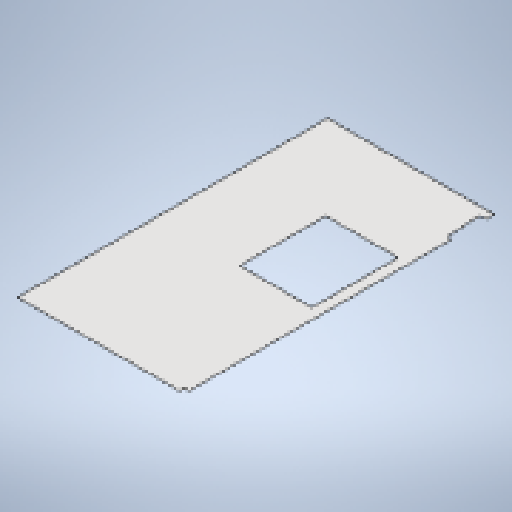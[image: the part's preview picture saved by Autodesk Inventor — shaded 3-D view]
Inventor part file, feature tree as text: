
AUTODESK INVENTOR PART (.ipt)
format: ipt  version: 2025.1 (Build 291241020, 241B)  size: 218,624 bytes
history: native  units: mm
features: other x2, sheet_metal_op x1, chamfer x1, sketch x1
ambient origin geometry x8: Origin, YZ Plane, XZ Plane, XY Plane, X Axis, Y Axis, Z Axis, Center Point
bodies: Body1 (feature_tree)
feature tree (5):
  sheet_metal_op  "Face3"
  chamfer  "Corner Round1"
  sketch  "Sketch1"  dims[d61=500.0mm d154=1385.0mm d155=2575.0mm d156=2.0mm d157=40.0mm d158=15.0mm d159=290.0mm d161=40.0mm d162=2220.0mm d163=10.0mm d164=150.0mm d165=5.0mm d166=590.0mm d167=590.0mm d168=675.0mm d169=520.0mm]
  other  "Plate5"
  other  "Definition1"
